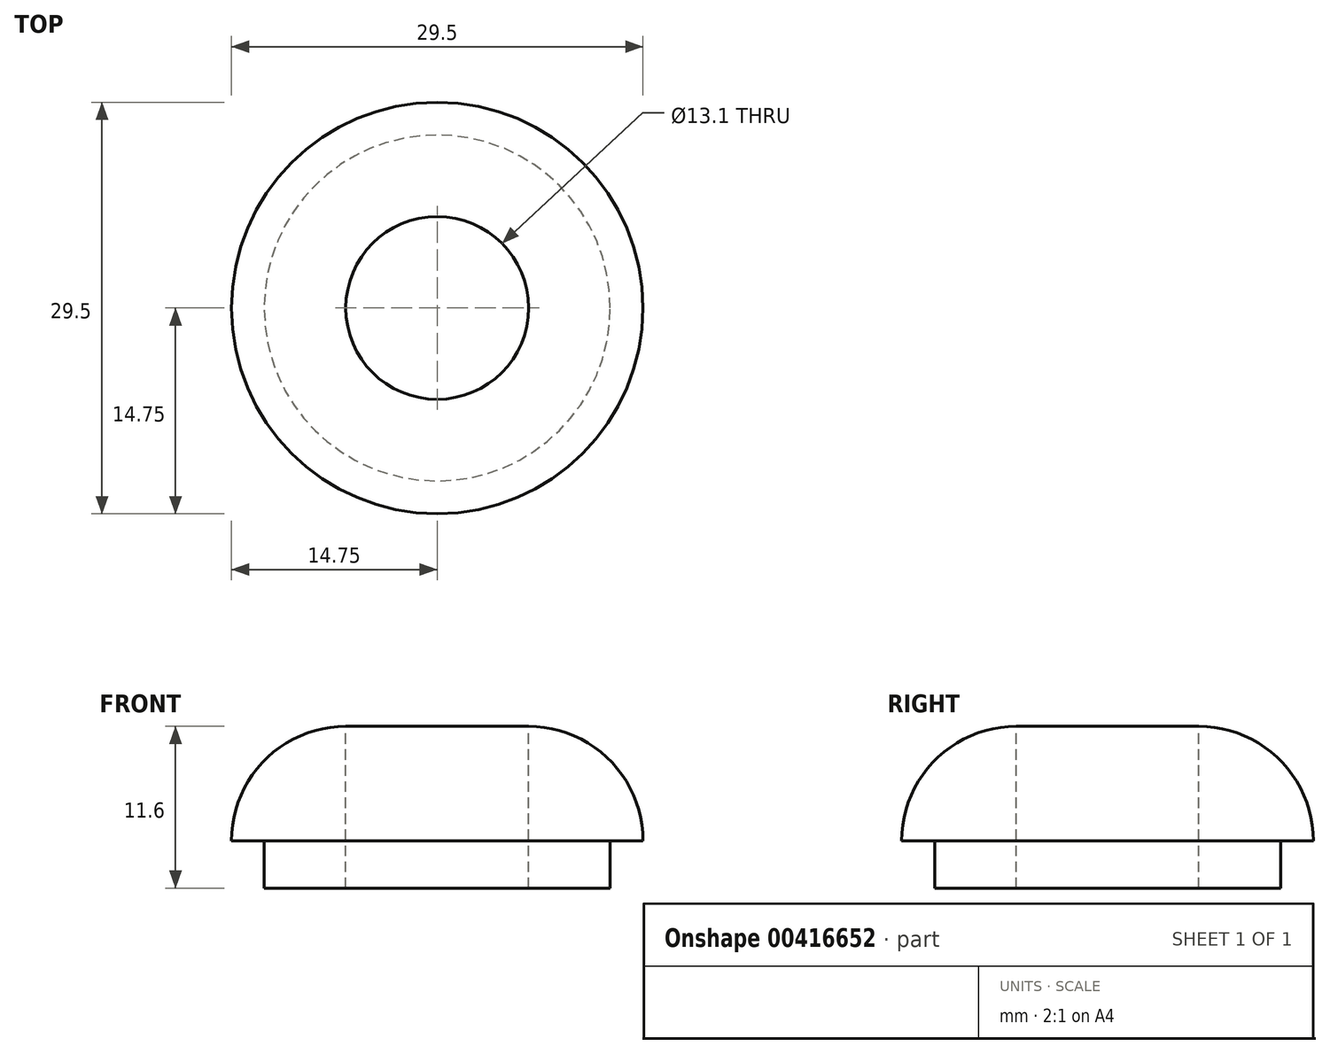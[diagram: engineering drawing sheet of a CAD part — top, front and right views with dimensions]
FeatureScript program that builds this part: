
annotation { "Feature Type Name" : "Feature", "Feature Type Description" : "" }
export const myFeature = defineFeature(function(context is Context, id is Id, definition is map)
    precondition{}
    {
        {
            var Q0;
            Q0=qCreatedBy(makeId("Top.planeOp"),FACE);
            var sketch = newSketch(context, id + "F0", { "sketchPlane" : qUnion([Q0])});
            skCircle(sketch, "E0", {"center": v(0, 0) * mm, "radius": 12.4 * mm});
            skCircle(sketch, "E1", {"center": v(0, 0) * mm, "radius": 14.75 * mm});
            skCircle(sketch, "E2", {"center": v(0, 0) * mm, "radius": 6.55 * mm});
            skCircle(sketch, "E3", {"center": v(0, 0) * mm, "radius": 2.08 * mm});
            skSolve(sketch);
        }
        {
            var Q0;
            Q0=makeQuery(id+"F0.imprint","IMPRINT",FACE,{"disambiguationData":[TD([[makeQuery(id+"F0.imprint","IMPRINT",EDGE,{"derivedFrom":sQuery(id+"F0.wireOp",EDGE,"E0")}),1.0]])]});
            extrude(context, id + "F1", {"entities" : qUnion([Q0]), "depth" : -3.4 * mm});
        }
        {
            var Q0;
            Q0 = qSketchRegion(id + "F0", true);
            var Q1;
            Q1=makeQuery(id+"F1.opExtrude","CAP_FACE",FACE,{"disambiguationData":[OSD([sQuery(id+"F0.wireOp",EDGE,"E0"),sQuery(id+"F0.wireOp",EDGE,"E2")])],"isStart":true});
            extrude(context, id + "F2", {"entities" : qUnion([Q0, Q1]), "operationType" : NewBodyOperationType.ADD, "depth" : 8.2 * mm});
        }
        {
            var Q0;
            Q0=makeQuery(id+"F2.opExtrude","CAP_EDGE",EDGE,{"disambiguationData":[OSD([sQuery(id+"F0.wireOp",EDGE,"E1")])],"isStart":false});
            fillet(context, id + "F3", {"entities" : qUnion([Q0]), "radius" : 8.2 * mm, "tangentPropagation" : true, "allowEdgeOverflow" : false});
        }
    });
